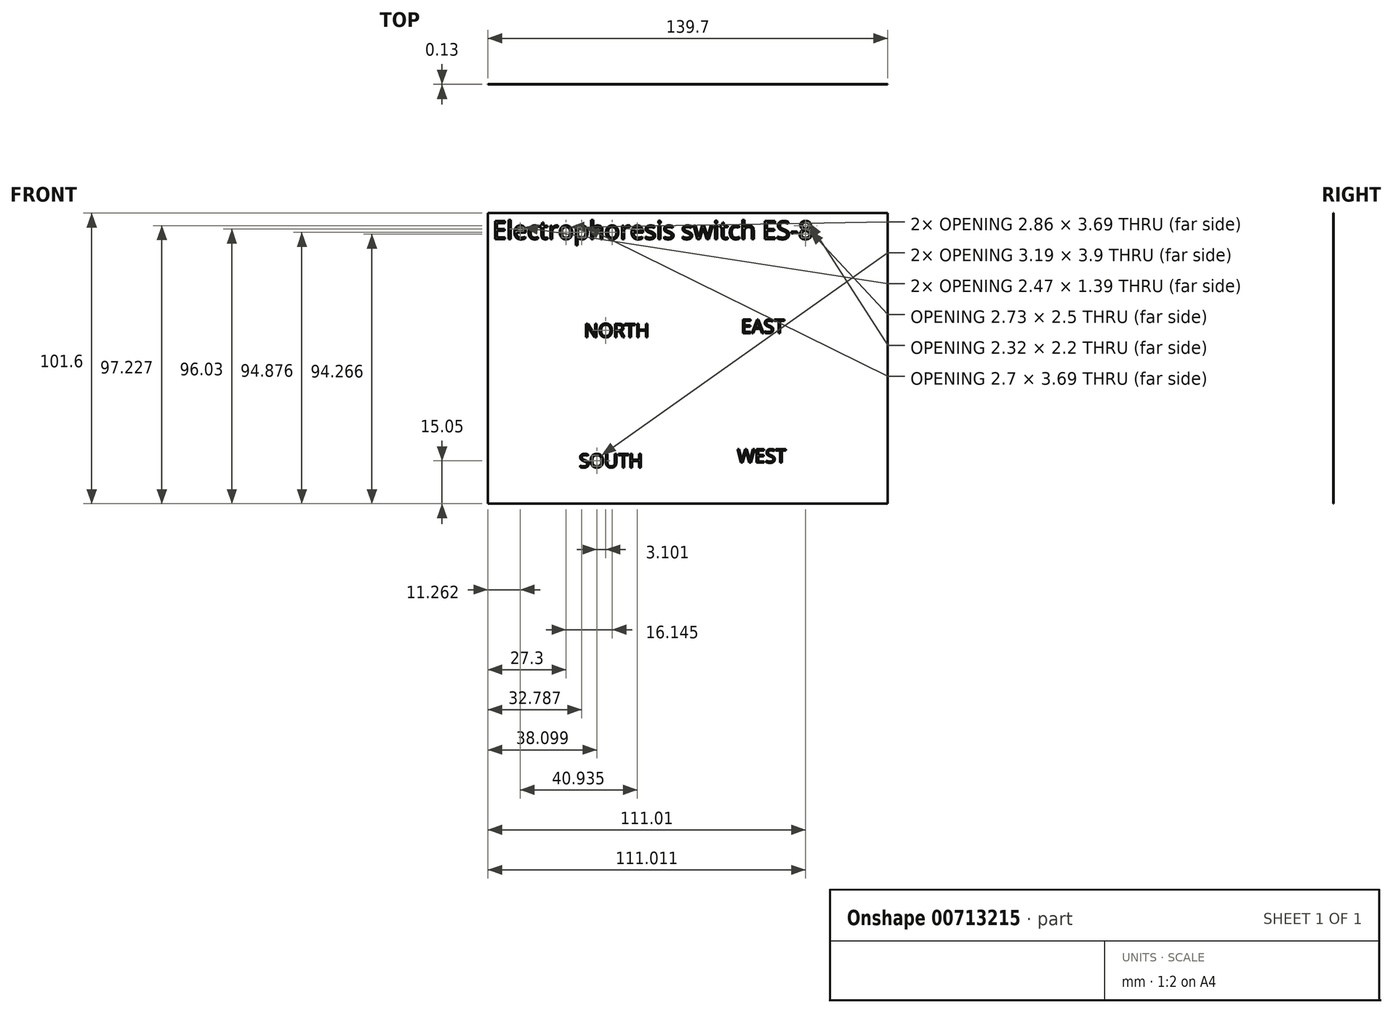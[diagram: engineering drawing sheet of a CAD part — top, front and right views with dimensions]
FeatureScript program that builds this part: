
annotation { "Feature Type Name" : "Feature", "Feature Type Description" : "" }
export const myFeature = defineFeature(function(context is Context, id is Id, definition is map)
    precondition{}
    {
        {
            var Q0;
            Q0=qCreatedBy(makeId("Front.planeOp"),FACE);
            var sketch = newSketch(context, id + "F0", { "sketchPlane" : qUnion([Q0])});
            skLineSegment(sketch, "E0.bottom", {"start": v(-69.85, 50.8) * mm, "end": v(69.85, 50.8) * mm});
            skLineSegment(sketch, "E0.top", {"start": v(-69.85, -50.8) * mm, "end": v(69.85, -50.8) * mm});
            skLineSegment(sketch, "E0.left", {"start": v(-69.85, 50.8) * mm, "end": v(-69.85, -50.8) * mm});
            skLineSegment(sketch, "E0.right", {"start": v(69.85, 50.8) * mm, "end": v(69.85, -50.8) * mm});
            skPoint(sketch, "E1", {"position": v(0, -50.8) * mm});
            skPoint(sketch, "E2", {"position": v(-69.85, 0) * mm});
            skSolve(sketch);
        }
        {
            var Q0;
            Q0 = qSketchRegion(id + "F0", true);
            extrude(context, id + "F1", {"entities" : qUnion([Q0]), "depth" : 0.13 * mm, "offsetDistance" : 25.4 * mm});
        }
        {
            var Q0;
            Q0=qCreatedBy(makeId("Front.planeOp"),FACE);
            var sketch = newSketch(context, id + "F2", { "sketchPlane" : qUnion([Q0])});
            skText(sketch, "E3", { "text": "NORTH", "fontName": "OpenSans-Regular.ttf"});
            skText(sketch, "E4", { "text": "EAST", "fontName": "OpenSans-Regular.ttf"});
            skText(sketch, "E5", { "text": "SOUTH\n", "fontName": "OpenSans-Regular.ttf"});
            skText(sketch, "E6", { "text": "WEST", "fontName": "OpenSans-Regular.ttf"});
            const initialGuessF2  = {"E3": [-0.03624, 0.00743, 1, 0, 0.00478], "E4": [0.01864, 0.00886, 1, 0, 0.00478], "E5": [-0.03798, -0.03812, 1, 0, 0.00478], "E6": [0.01726, -0.03644, 1, 0, 0.00478]};
            skSetInitialGuess(sketch, initialGuessF2);
            skSolve(sketch);
        }
        {
            var Q0;
            Q0=qCreatedBy(makeId("Front.planeOp"),FACE);
            var sketch = newSketch(context, id + "F3", { "sketchPlane" : qUnion([Q0])});
            skText(sketch, "E7", { "text": "Electrophoresis switch ES-8", "fontName": "OpenSans-Regular.ttf"});
            const initialGuessF3  = {"E7": [-0.06821, 0.04172, 1, 0, 0.00635]};
            skSetInitialGuess(sketch, initialGuessF3);
            skSolve(sketch);
        }
        {
            var Q0;
            Q0 = qSketchRegion(id + "F2", true);
            var Q1;
            Q1 = qSketchRegion(id + "F3", true);
            extrude(context, id + "F4", {"entities" : qUnion([Q0, Q1]), "depth" : 0.13 * mm, "offsetDistance" : 25.4 * mm});
        }
    });
